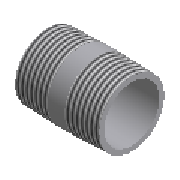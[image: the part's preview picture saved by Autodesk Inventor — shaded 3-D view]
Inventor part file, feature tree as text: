
AUTODESK INVENTOR PART (.ipt)
format: ipt  version: 2023.2 (Build 272271030, 271C)  size: 182,784 bytes
history: native  units: mm (DEFAULTED — no unit token found)
features: other x6, revolve x1, sketch x1
ambient origin geometry x8: Origin, YZ Plane, XZ Plane, XY Plane, X Axis, Y Axis, Z Axis, Center Point
bodies: Solid1 (feature_tree)
feature tree (8):
  revolve  "Revolution1"  [1 undecoded]
  other  "Work Point3"
  other  "Work Point4"
  other  "Work Axis1"
  other  "Work Point5"
  other  "Work Axis2"
  other  "Work Point6"
  sketch  "Sketch1"  dims[d12=90.0deg d1=0.312398mm d2=42.0mm d3=18.9mm d4=0.0mm d5=18.9mm d6=0.0mm d7=10.39mm d8=33.249mm d57=27.6mm d60=16.79mm d62=0.0mm]
note: 1 required parameter value undecoded (feature->parameter linkage not recoverable at this tier; creation-order binding heuristic only, values carry confidence <= 0.55)
